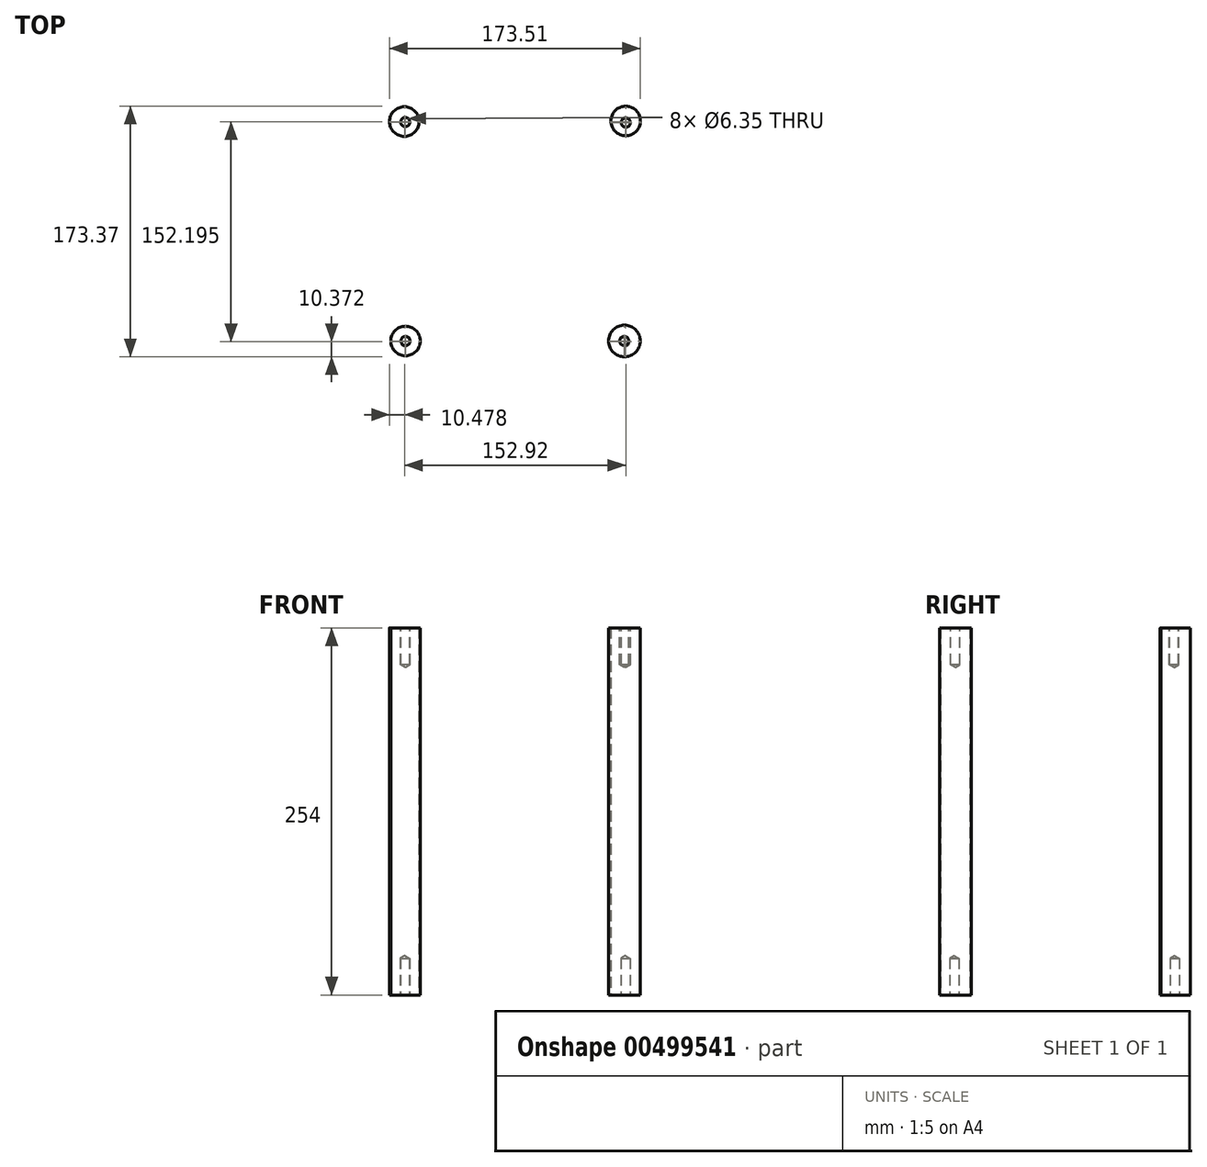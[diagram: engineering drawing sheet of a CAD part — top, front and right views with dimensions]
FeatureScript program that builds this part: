
annotation { "Feature Type Name" : "Feature", "Feature Type Description" : "" }
export const myFeature = defineFeature(function(context is Context, id is Id, definition is map)
    precondition{}
    {
        {
            var Q0;
            Q0=qCreatedBy(makeId("Top.planeOp"),FACE);
            var sketch = newSketch(context, id + "F0", { "sketchPlane" : qUnion([Q0])});
            skPoint(sketch, "E0", {"position": v(-76.73, 76.1) * mm});
            skPoint(sketch, "E1", {"position": v(76.32, 76.53) * mm});
            skPoint(sketch, "E2", {"position": v(75.49, -75.7) * mm});
            skPoint(sketch, "E3", {"position": v(-75.9, -75.7) * mm});
            skCircle(sketch, "E4", {"center": v(-76.73, 76.1) * mm, "radius": 10.25 * mm});
            skCircle(sketch, "E5", {"center": v(76.32, 76.53) * mm, "radius": 10.2 * mm});
            skCircle(sketch, "E6", {"center": v(-75.9, -75.7) * mm, "radius": 10.21 * mm});
            skCircle(sketch, "E7", {"center": v(75.49, -75.7) * mm, "radius": 10.95 * mm});
            skSolve(sketch);
        }
        {
            var Q0;
            Q0=makeQuery(id+"F0.imprint","IMPRINT",FACE,{"disambiguationData":[TD([[makeQuery(id+"F0.imprint","IMPRINT",EDGE,{"derivedFrom":sQuery(id+"F0.wireOp",EDGE,"E4")}),1.0]])]});
            var Q1;
            Q1=makeQuery(id+"F0.imprint","IMPRINT",FACE,{"disambiguationData":[TD([[makeQuery(id+"F0.imprint","IMPRINT",EDGE,{"derivedFrom":sQuery(id+"F0.wireOp",EDGE,"E5")}),1.0]])]});
            var Q2;
            Q2=makeQuery(id+"F0.imprint","IMPRINT",FACE,{"disambiguationData":[TD([[makeQuery(id+"F0.imprint","IMPRINT",EDGE,{"derivedFrom":sQuery(id+"F0.wireOp",EDGE,"E7")}),1.0]])]});
            var Q3;
            Q3=makeQuery(id+"F0.imprint","IMPRINT",FACE,{"disambiguationData":[TD([[makeQuery(id+"F0.imprint","IMPRINT",EDGE,{"derivedFrom":sQuery(id+"F0.wireOp",EDGE,"E6")}),1.0]])]});
            extrude(context, id + "F1", {"entities" : qUnion([Q0, Q1, Q2, Q3]), "depth" : 254 * mm, "offsetDistance" : 25.4 * mm});
        }
        {
            var Q0;
            Q0=makeQuery(id+"F1.opExtrude","CAP_FACE",FACE,{"disambiguationData":[OSD([sQuery(id+"F0.wireOp",EDGE,"E6")])],"isStart":false});
            var sketch = newSketch(context, id + "F2", { "sketchPlane" : qUnion([Q0])});
            skPoint(sketch, "E8", {"position": v(-76.08, 75.72) * mm});
            skPoint(sketch, "E9", {"position": v(76.42, 75.36) * mm});
            skPoint(sketch, "E10", {"position": v(75.33, -75.7) * mm});
            skPoint(sketch, "E11", {"position": v(-75.9, -75.7) * mm});
            skSolve(sketch);
        }
        {
            var Q0;
            Q0=sQuery(id+"F2.wireOp",VERTEX,"E8");
            var Q1;
            Q1=sQuery(id+"F2.wireOp",VERTEX,"E9");
            var Q2;
            Q2=sQuery(id+"F2.wireOp",VERTEX,"E10");
            var Q3;
            Q3=sQuery(id+"F2.wireOp",VERTEX,"E11");
            var Q4;
            Q4=makeQuery(id+"F1.opExtrude","SWEPT_BODY",BODY,{"disambiguationData":[OSD([sQuery(id+"F0.wireOp",EDGE,"E4")])]});
            var Q5;
            Q5=makeQuery(id+"F1.opExtrude","SWEPT_BODY",BODY,{"disambiguationData":[OSD([sQuery(id+"F0.wireOp",EDGE,"E5")])]});
            var Q6;
            Q6=makeQuery(id+"F1.opExtrude","SWEPT_BODY",BODY,{"disambiguationData":[OSD([sQuery(id+"F0.wireOp",EDGE,"E7")])]});
            var Q7;
            Q7=makeQuery(id+"F1.opExtrude","SWEPT_BODY",BODY,{"disambiguationData":[OSD([sQuery(id+"F0.wireOp",EDGE,"E6")])]});
            hole(context, id + "F3", {"style" : HoleStyle.SIMPLE, "endStyle" : HoleEndStyle.BLIND, "holeDiameter" : 6.35 * mm, "holeDepth" : 25.4 * mm, "isTappedThrough" : true, "tappedDepth" : 12.7 * mm, "tapClearance" : 3, "locations" : qUnion([Q0, Q1, Q2, Q3]), "scope" : qUnion([Q4, Q5, Q6, Q7])});
        }
        {
            var Q0;
            Q0=qCreatedBy(makeId("Top.planeOp"),FACE);
            var sketch = newSketch(context, id + "F4", { "sketchPlane" : qUnion([Q0])});
            skPoint(sketch, "E12", {"position": v(-76.23, -76.27) * mm});
            skPoint(sketch, "E13", {"position": v(76.09, -76.27) * mm});
            skPoint(sketch, "E14", {"position": v(-76.5, 75.93) * mm});
            skPoint(sketch, "E15", {"position": v(76.18, 75.89) * mm});
            skSolve(sketch);
        }
        {
            var Q0;
            Q0=sQuery(id+"F4.wireOp",VERTEX,"E12");
            var Q1;
            Q1=sQuery(id+"F4.wireOp",VERTEX,"E13");
            var Q2;
            Q2=sQuery(id+"F4.wireOp",VERTEX,"E15");
            var Q3;
            Q3=sQuery(id+"F4.wireOp",VERTEX,"E14");
            var Q4;
            Q4=makeQuery(id+"F1.opExtrude","SWEPT_BODY",BODY,{"disambiguationData":[OSD([sQuery(id+"F0.wireOp",EDGE,"E4")])]});
            var Q5;
            Q5=makeQuery(id+"F1.opExtrude","SWEPT_BODY",BODY,{"disambiguationData":[OSD([sQuery(id+"F0.wireOp",EDGE,"E5")])]});
            var Q6;
            Q6=makeQuery(id+"F1.opExtrude","SWEPT_BODY",BODY,{"disambiguationData":[OSD([sQuery(id+"F0.wireOp",EDGE,"E6")])]});
            var Q7;
            Q7=makeQuery(id+"F1.opExtrude","SWEPT_BODY",BODY,{"disambiguationData":[OSD([sQuery(id+"F0.wireOp",EDGE,"E7")])]});
            hole(context, id + "F5", {"style" : HoleStyle.SIMPLE, "endStyle" : HoleEndStyle.BLIND, "oppositeDirection" : true, "holeDiameter" : 6.35 * mm, "holeDepth" : 25.4 * mm, "isTappedThrough" : true, "tappedDepth" : 12.7 * mm, "tapClearance" : 3, "locations" : qUnion([Q0, Q1, Q2, Q3]), "scope" : qUnion([Q4, Q5, Q6, Q7])});
        }
    });
